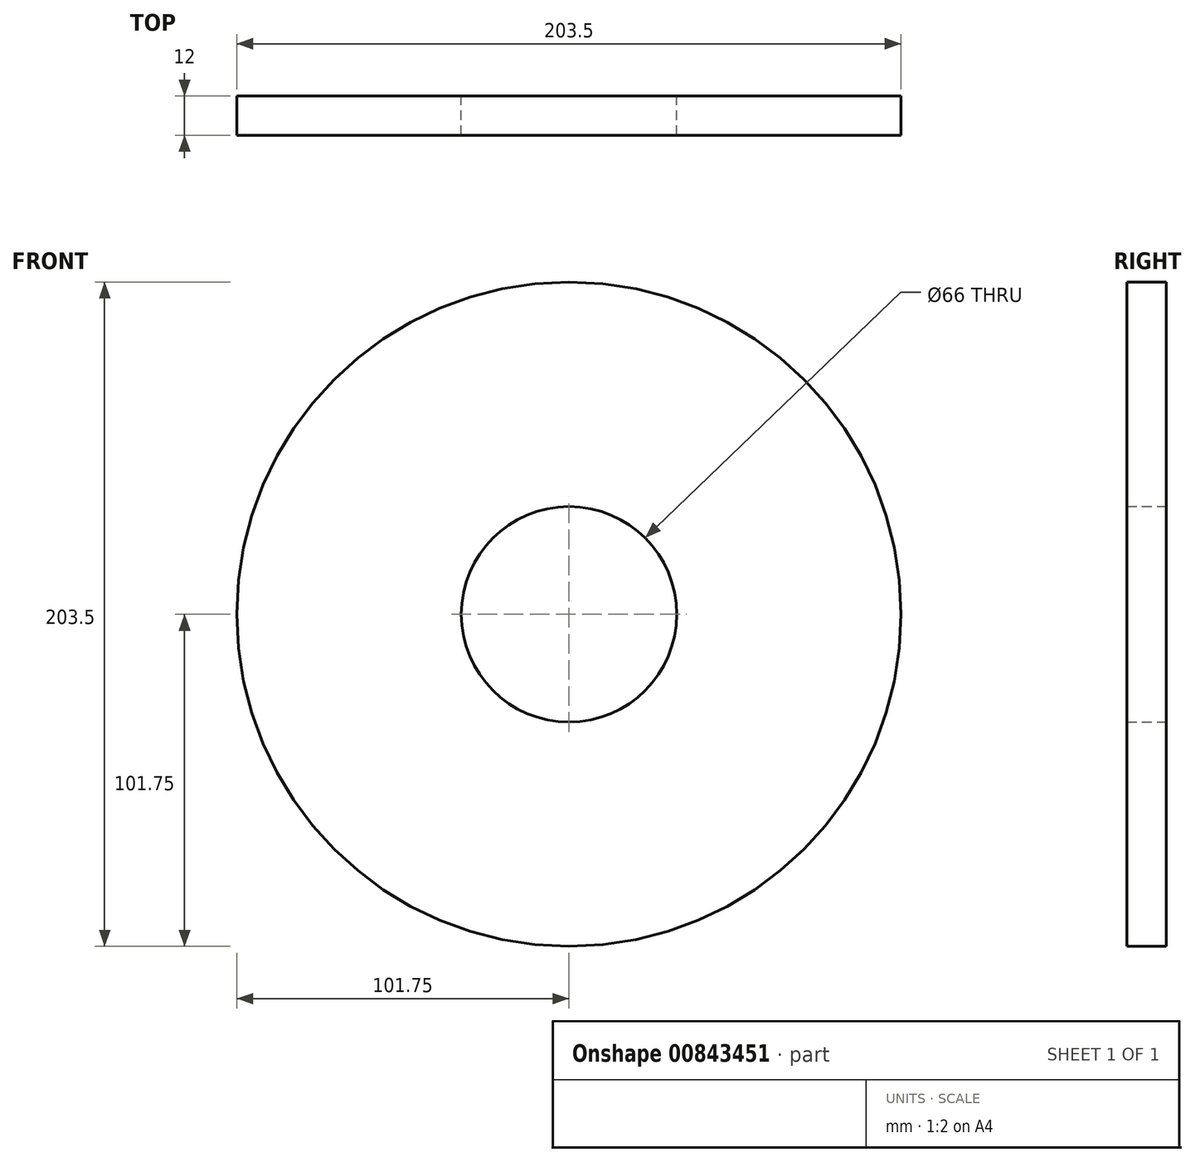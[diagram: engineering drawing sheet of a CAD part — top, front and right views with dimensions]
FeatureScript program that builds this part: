
annotation { "Feature Type Name" : "Feature", "Feature Type Description" : "" }
export const myFeature = defineFeature(function(context is Context, id is Id, definition is map)
    precondition{}
    {
        {
            var Q0;
            Q0=qCreatedBy(makeId("Front.planeOp"),FACE);
            var sketch = newSketch(context, id + "F0", { "sketchPlane" : qUnion([Q0])});
            skCircle(sketch, "E0", {"center": v(0, 0) * mm, "radius": 33 * mm});
            skCircle(sketch, "E1", {"center": v(0, 0) * mm, "radius": 101.75 * mm});
            skSolve(sketch);
        }
        {
            var Q0;
            Q0=makeQuery(id+"F0.imprint","IMPRINT",FACE,{"disambiguationData":[TD([[makeQuery(id+"F0.imprint","IMPRINT",EDGE,{"derivedFrom":sQuery(id+"F0.wireOp",EDGE,"E0")}),-1.0]])]});
            extrude(context, id + "F1", {"entities" : qUnion([Q0]), "depth" : 12 * mm, "offsetDistance" : 25 * mm});
        }
    });
